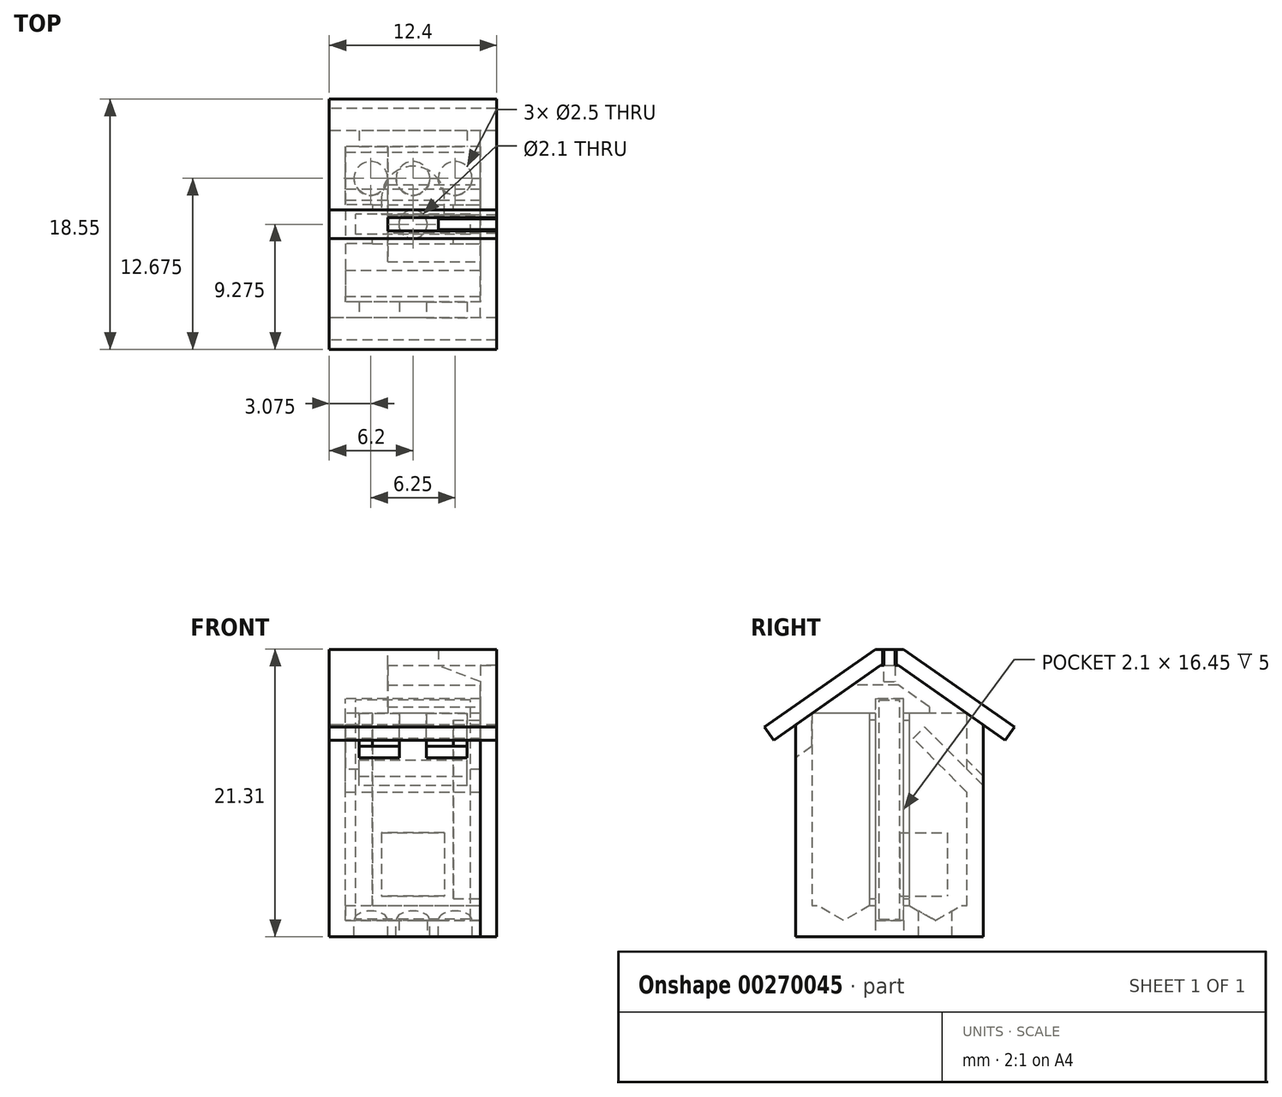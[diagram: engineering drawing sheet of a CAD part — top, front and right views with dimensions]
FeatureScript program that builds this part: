
annotation { "Feature Type Name" : "Feature", "Feature Type Description" : "" }
export const myFeature = defineFeature(function(context is Context, id is Id, definition is map)
    precondition{}
    {
        {
            var Q0;
            Q0=qCreatedBy(makeId("Top.planeOp"),FACE);
            var sketch = newSketch(context, id + "F0", { "sketchPlane" : qUnion([Q0])});
            skArc(sketch, "E0", {"start": v(2.33, 0) * mm, "mid": v(0, 2.33) * mm, "end": v(-2.33, 0) * mm});
            skLineSegment(sketch, "E1", {"start": v(-2.33, 0) * mm, "end": v(-2.33, -1.23) * mm});
            skLineSegment(sketch, "E2", {"start": v(-2.32, -1.23) * mm, "end": v(2.32, -1.22) * mm});
            skLineSegment(sketch, "E3", {"start": v(2.33, -1.23) * mm, "end": v(2.33, 0) * mm});
            skSolve(sketch);
        }
        {
            var Q0;
            Q0 = qSketchRegion(id + "F0", true);
            extrude(context, id + "F1", {"entities" : qUnion([Q0]), "endBound" : BoundingType.SYMMETRIC, "depth" : 4.7 * mm});
        }
        {
            var Q0;
            Q0=makeQuery(id+"F1.opExtrude","CAP_FACE",FACE,{"disambiguationData":[OSD([sQuery(id+"F0.wireOp",EDGE,"E0"),sQuery(id+"F0.wireOp",EDGE,"E1"),sQuery(id+"F0.wireOp",EDGE,"E2"),sQuery(id+"F0.wireOp",EDGE,"E3")])],"isStart":false});
            var sketch = newSketch(context, id + "F2", { "sketchPlane" : qUnion([Q0])});
            skLineSegment(sketch, "E4.bottom", {"start": v(1.88, 0.45) * mm, "end": v(-1.87, 0.45) * mm});
            skLineSegment(sketch, "E4.top", {"start": v(1.88, -0.45) * mm, "end": v(-1.88, -0.45) * mm});
            skLineSegment(sketch, "E4.left", {"start": v(1.88, 0.45) * mm, "end": v(1.88, -0.45) * mm});
            skLineSegment(sketch, "E4.right", {"start": v(-1.88, 0.45) * mm, "end": v(-1.88, -0.45) * mm});
            skPoint(sketch, "E4.middle", {"position": v(0, 0) * mm});
            skSolve(sketch);
        }
        {
            var Q0;
            Q0=makeQuery(id+"F1.opExtrude","SWEPT_FACE",FACE,{"disambiguationData":[OSD([sQuery(id+"F0.wireOp",EDGE,"E2")])]});
            var sketch = newSketch(context, id + "F3", { "sketchPlane" : qUnion([Q0])});
            skLineSegment(sketch, "E5.bottom", {"start": v(4.25, -4.05) * mm, "end": v(-4.25, -4.05) * mm});
            skLineSegment(sketch, "E5.top", {"start": v(4.25, 12.2) * mm, "end": v(-4.25, 12.2) * mm});
            skLineSegment(sketch, "E5.left", {"start": v(4.25, -4.05) * mm, "end": v(4.25, 12.2) * mm});
            skLineSegment(sketch, "E5.right", {"start": v(-4.25, -4.05) * mm, "end": v(-4.25, 12.2) * mm});
            skPoint(sketch, "E5.middle", {"position": v(0, 4.08) * mm});
            skSolve(sketch);
        }
        {
            var Q0;
            Q0 = qSketchRegion(id + "F3", true);
            extrude(context, id + "F4", {"entities" : qUnion([Q0]), "operationType" : NewBodyOperationType.ADD, "depth" : 1.5 * mm});
        }
        {
            var Q0;
            Q0=qCreatedBy(makeId("Right.planeOp"),FACE);
            var sketch = newSketch(context, id + "F5", { "sketchPlane" : qUnion([Q0])});
            skLineSegment(sketch, "E6", {"start": v(-3.02, -4.15) * mm, "end": v(-0.92, -4.15) * mm});
            skLineSegment(sketch, "E7", {"start": v(-0.92, -4.15) * mm, "end": v(-0.92, -3.05) * mm});
            skLineSegment(sketch, "E8", {"start": v(-0.92, -3.05) * mm, "end": v(3.78, -3.05) * mm});
            skLineSegment(sketch, "E9", {"start": v(3.78, -3.05) * mm, "end": v(3.78, 11.2) * mm});
            skLineSegment(sketch, "E10", {"start": v(3.78, 11.2) * mm, "end": v(-0.92, 11.2) * mm});
            skLineSegment(sketch, "E11", {"start": v(-0.92, 11.2) * mm, "end": v(-0.92, 12.3) * mm});
            skLineSegment(sketch, "E12", {"start": v(-0.92, 12.3) * mm, "end": v(-3.02, 12.3) * mm});
            skLineSegment(sketch, "E13", {"start": v(-3.02, 12.3) * mm, "end": v(-3.02, 11.2) * mm});
            skLineSegment(sketch, "E14", {"start": v(-3.02, 11.2) * mm, "end": v(-7.72, 11.2) * mm});
            skLineSegment(sketch, "E15", {"start": v(-7.72, 11.2) * mm, "end": v(-7.72, -3.05) * mm});
            skLineSegment(sketch, "E16", {"start": v(-7.72, -3.05) * mm, "end": v(-3.02, -3.05) * mm});
            skLineSegment(sketch, "E17", {"start": v(-3.02, -3.05) * mm, "end": v(-3.02, -4.15) * mm});
            skLineSegment(sketch, "E18", {"start": v(-3.02, 15.96) * mm, "end": v(-11.25, 10.2) * mm});
            skLineSegment(sketch, "E19", {"start": v(-11.25, 10.2) * mm, "end": v(-10.56, 9.21) * mm});
            skLineSegment(sketch, "E20", {"start": v(-10.56, 9.21) * mm, "end": v(-8.92, 10.36) * mm});
            skLineSegment(sketch, "E21", {"start": v(-8.92, 10.36) * mm, "end": v(-8.92, -5.35) * mm});
            skLineSegment(sketch, "E22", {"start": v(-8.92, -5.35) * mm, "end": v(4.98, -5.35) * mm});
            skLineSegment(sketch, "E23", {"start": v(4.98, -5.35) * mm, "end": v(4.98, 10.36) * mm});
            skLineSegment(sketch, "E24", {"start": v(4.98, 10.36) * mm, "end": v(6.61, 9.21) * mm});
            skLineSegment(sketch, "E25", {"start": v(6.61, 9.21) * mm, "end": v(7.3, 10.2) * mm});
            skLineSegment(sketch, "E26", {"start": v(7.3, 10.2) * mm, "end": v(-0.92, 15.96) * mm});
            skLineSegment(sketch, "E27", {"start": v(-0.92, 15.96) * mm, "end": v(-3.02, 15.96) * mm});
            skLineSegment(sketch, "E28", {"start": v(-8.92, 10.36) * mm, "end": v(-7.72, 11.2) * mm, "construction": true});
            skSolve(sketch);
        }
        {
            var Q0;
            Q0=makeQuery(id+"F5.imprint","IMPRINT",FACE,{"disambiguationData":[TD([[makeQuery(id+"F5.imprint","IMPRINT",EDGE,{"derivedFrom":sQuery(id+"F5.wireOp",EDGE,"E6")}),-1.0]])]});
            extrude(context, id + "F6", {"entities" : qUnion([Q0]), "endBound" : BoundingType.SYMMETRIC, "depth" : 10 * mm});
        }
        {
            var Q0;
            Q0=makeQuery(id+"F6.opExtrude","SWEPT_FACE",FACE,{"disambiguationData":[OSD([sQuery(id+"F5.wireOp",EDGE,"E19")])]});
            var sketch = newSketch(context, id + "F7", { "sketchPlane" : qUnion([Q0])});
            skLineSegment(sketch, "E29.bottom", {"start": v(-4, 13.6) * mm, "end": v(-1, 13.6) * mm});
            skLineSegment(sketch, "E29.top", {"start": v(-4, 11.6) * mm, "end": v(-1, 11.6) * mm});
            skLineSegment(sketch, "E29.left", {"start": v(-4, 13.6) * mm, "end": v(-4, 11.6) * mm});
            skLineSegment(sketch, "E29.right", {"start": v(-1, 13.6) * mm, "end": v(-1, 11.6) * mm});
            skLineSegment(sketch, "E30.bottom", {"start": v(4, 13.6) * mm, "end": v(1, 13.6) * mm});
            skLineSegment(sketch, "E30.top", {"start": v(4, 11.6) * mm, "end": v(1, 11.6) * mm});
            skLineSegment(sketch, "E30.left", {"start": v(4, 13.6) * mm, "end": v(4, 11.6) * mm});
            skLineSegment(sketch, "E30.right", {"start": v(1, 13.6) * mm, "end": v(1, 11.6) * mm});
            skSolve(sketch);
        }
        {
            var Q0;
            Q0 = qSketchRegion(id + "F7", true);
            var Q1;
            Q1=makeQuery(id+"F6.opExtrude","SWEPT_FACE",FACE,{"disambiguationData":[OSD([sQuery(id+"F5.wireOp",EDGE,"E14")])]});
            extrude(context, id + "F8", {"entities" : qUnion([Q0]), "operationType" : NewBodyOperationType.REMOVE, "endBound" : BoundingType.UP_TO_SURFACE, "oppositeDirection" : true, "endBoundEntityFace" : qUnion([Q1]), "depth" : 25 * mm});
        }
        {
            var Q0;
            Q0=makeQuery(id+"F4.opExtrude","SWEPT_EDGE",EDGE,{"disambiguationData":[OSD([sQuery(id+"F3.wireOp",EDGE,"E5.top"),sQuery(id+"F3.wireOp",EDGE,"E5.left")])]});
            cPoint(context, id + "F9", {"entities" : qUnion([Q0]), "parameter" : 0.5});
        }
        {
            var Q0;
            Q0=makeQuery(id+"F4.opExtrude","SWEPT_EDGE",EDGE,{"disambiguationData":[OSD([sQuery(id+"F3.wireOp",EDGE,"E5.bottom"),sQuery(id+"F3.wireOp",EDGE,"E5.left")])]});
            cPoint(context, id + "F10", {"entities" : qUnion([Q0]), "parameter" : 0.5});
        }
        {
            var Q0;
            Q0=makeQuery(id+"F4.opExtrude","SWEPT_EDGE",EDGE,{"disambiguationData":[OSD([sQuery(id+"F3.wireOp",EDGE,"E5.bottom"),sQuery(id+"F3.wireOp",EDGE,"E5.right")])]});
            cPoint(context, id + "F11", {"entities" : qUnion([Q0]), "parameter" : 0.5});
        }
        {
            var Q0;
            Q0 = qCreatedBy(id + "F9" ,VERTEX);
            var Q1;
            Q1 = qCreatedBy(id + "F10" ,VERTEX);
            var Q2;
            Q2 = qCreatedBy(id + "F11" ,VERTEX);
            cPlane(context, id + "F12", {"entities" : qUnion([Q0, Q1, Q2]), "cplaneType" : CPlaneType.THREE_POINT, "offset" : 25 * mm, "width" : 150 * mm, "height" : 150 * mm});
        }
        {
            var Q0;
            Q0=makeQuery(id+"F6.opExtrude","SWEPT_FACE",FACE,{"disambiguationData":[OSD([sQuery(id+"F5.wireOp",EDGE,"E16")])]});
            var sketch = newSketch(context, id + "F13", { "sketchPlane" : qUnion([Q0])});
            skCircle(sketch, "E31", {"center": v(-3.12, 1.43) * mm, "radius": 1.25 * mm});
            skCircle(sketch, "E32", {"center": v(0, 1.43) * mm, "radius": 1.25 * mm});
            skCircle(sketch, "E33", {"center": v(3.12, 1.43) * mm, "radius": 1.25 * mm});
            skLineSegment(sketch, "E34", {"start": v(-3.12, 1.43) * mm, "end": v(-5, 1.43) * mm, "construction": true});
            skLineSegment(sketch, "E35", {"start": v(-3.12, 1.43) * mm, "end": v(-1.25, 1.43) * mm, "construction": true});
            skSolve(sketch);
        }
        {
            var Q0;
            Q0 = qSketchRegion(id + "F13", true);
            extrude(context, id + "F14", {"entities" : qUnion([Q0]), "operationType" : NewBodyOperationType.REMOVE, "endBound" : BoundingType.THROUGH_ALL, "oppositeDirection" : true, "depth" : 25 * mm});
        }
        {
            var Q0;
            Q0=makeQuery(id+"F6.opExtrude","CAP_FACE",FACE,{"disambiguationData":[OSD([sQuery(id+"F5.wireOp",EDGE,"E6"),sQuery(id+"F5.wireOp",EDGE,"E7"),sQuery(id+"F5.wireOp",EDGE,"E8"),sQuery(id+"F5.wireOp",EDGE,"E9"),sQuery(id+"F5.wireOp",EDGE,"E10"),sQuery(id+"F5.wireOp",EDGE,"E11"),sQuery(id+"F5.wireOp",EDGE,"E12"),sQuery(id+"F5.wireOp",EDGE,"E13"),sQuery(id+"F5.wireOp",EDGE,"E14"),sQuery(id+"F5.wireOp",EDGE,"E15"),sQuery(id+"F5.wireOp",EDGE,"E16"),sQuery(id+"F5.wireOp",EDGE,"E17"),sQuery(id+"F5.wireOp",EDGE,"E18"),sQuery(id+"F5.wireOp",EDGE,"E19"),sQuery(id+"F5.wireOp",EDGE,"E20"),sQuery(id+"F5.wireOp",EDGE,"E21"),sQuery(id+"F5.wireOp",EDGE,"E22"),sQuery(id+"F5.wireOp",EDGE,"E23"),sQuery(id+"F5.wireOp",EDGE,"E24"),sQuery(id+"F5.wireOp",EDGE,"E25"),sQuery(id+"F5.wireOp",EDGE,"E26"),sQuery(id+"F5.wireOp",EDGE,"E27")])],"isStart":true});
            var sketch = newSketch(context, id + "F15", { "sketchPlane" : qUnion([Q0])});
            skLineSegment(sketch, "E36.0.0", {"start": v(0.92, 15.96) * mm, "end": v(-7.3, 10.2) * mm});
            skLineSegment(sketch, "E36.0.1", {"start": v(-7.3, 10.2) * mm, "end": v(-6.61, 9.21) * mm});
            skLineSegment(sketch, "E36.0.2", {"start": v(-6.61, 9.21) * mm, "end": v(-4.98, 10.36) * mm});
            skLineSegment(sketch, "E36.0.3", {"start": v(-4.98, 10.36) * mm, "end": v(-4.98, -5.35) * mm});
            skLineSegment(sketch, "E36.0.4", {"start": v(-4.98, -5.35) * mm, "end": v(8.92, -5.35) * mm});
            skLineSegment(sketch, "E36.0.5", {"start": v(8.92, -5.35) * mm, "end": v(8.92, 10.36) * mm});
            skLineSegment(sketch, "E36.0.6", {"start": v(8.92, 10.36) * mm, "end": v(10.56, 9.21) * mm});
            skLineSegment(sketch, "E36.0.7", {"start": v(10.56, 9.21) * mm, "end": v(11.25, 10.2) * mm});
            skLineSegment(sketch, "E36.0.8", {"start": v(11.25, 10.2) * mm, "end": v(3.02, 15.96) * mm});
            skLineSegment(sketch, "E36.0.9", {"start": v(3.02, 15.96) * mm, "end": v(0.92, 15.96) * mm});
            skSolve(sketch);
        }
        {
            var Q0;
            Q0 = qSketchRegion(id + "F15", true);
            extrude(context, id + "F16", {"entities" : qUnion([Q0]), "operationType" : NewBodyOperationType.ADD, "depth" : 1.2 * mm});
        }
        {
            var Q0;
            Q0=makeQuery(id+"F6.opExtrude","CAP_FACE",FACE,{"disambiguationData":[OSD([sQuery(id+"F5.wireOp",EDGE,"E6"),sQuery(id+"F5.wireOp",EDGE,"E7"),sQuery(id+"F5.wireOp",EDGE,"E8"),sQuery(id+"F5.wireOp",EDGE,"E9"),sQuery(id+"F5.wireOp",EDGE,"E10"),sQuery(id+"F5.wireOp",EDGE,"E11"),sQuery(id+"F5.wireOp",EDGE,"E12"),sQuery(id+"F5.wireOp",EDGE,"E13"),sQuery(id+"F5.wireOp",EDGE,"E14"),sQuery(id+"F5.wireOp",EDGE,"E15"),sQuery(id+"F5.wireOp",EDGE,"E16"),sQuery(id+"F5.wireOp",EDGE,"E17"),sQuery(id+"F5.wireOp",EDGE,"E18"),sQuery(id+"F5.wireOp",EDGE,"E19"),sQuery(id+"F5.wireOp",EDGE,"E20"),sQuery(id+"F5.wireOp",EDGE,"E21"),sQuery(id+"F5.wireOp",EDGE,"E22"),sQuery(id+"F5.wireOp",EDGE,"E23"),sQuery(id+"F5.wireOp",EDGE,"E24"),sQuery(id+"F5.wireOp",EDGE,"E25"),sQuery(id+"F5.wireOp",EDGE,"E26"),sQuery(id+"F5.wireOp",EDGE,"E27")])],"isStart":false});
            var sketch = newSketch(context, id + "F17", { "sketchPlane" : qUnion([Q0])});
            skLineSegment(sketch, "E37", {"start": v(-3.02, 15.96) * mm, "end": v(-11.25, 10.2) * mm});
            skLineSegment(sketch, "E38", {"start": v(-11.25, 10.2) * mm, "end": v(-10.56, 9.21) * mm});
            skLineSegment(sketch, "E39", {"start": v(-10.56, 9.21) * mm, "end": v(-2.65, 14.76) * mm});
            skLineSegment(sketch, "E40", {"start": v(-2.65, 14.76) * mm, "end": v(-1.3, 14.76) * mm});
            skLineSegment(sketch, "E41", {"start": v(-1.3, 14.76) * mm, "end": v(6.61, 9.21) * mm});
            skLineSegment(sketch, "E42", {"start": v(6.61, 9.21) * mm, "end": v(7.3, 10.2) * mm});
            skLineSegment(sketch, "E43", {"start": v(7.3, 10.2) * mm, "end": v(-0.92, 15.96) * mm});
            skLineSegment(sketch, "E44", {"start": v(-0.92, 15.96) * mm, "end": v(-3.02, 15.96) * mm});
            skSolve(sketch);
        }
        {
            var Q0;
            Q0 = qSketchRegion(id + "F17", true);
            extrude(context, id + "F18", {"entities" : qUnion([Q0]), "operationType" : NewBodyOperationType.ADD, "depth" : 1.2 * mm});
        }
        {
            var Q0;
            {var subQ0=sQuery(id+"F5.wireOp",EDGE,"E24");var subQ1=sQuery(id+"F5.wireOp",EDGE,"E20");var subQ2=sQuery(id+"F5.wireOp",EDGE,"E14");var subQ3=sQuery(id+"F5.wireOp",EDGE,"E13");var subQ4=sQuery(id+"F5.wireOp",EDGE,"E12");var subQ5=sQuery(id+"F5.wireOp",EDGE,"E15");var subQ6=sQuery(id+"F5.wireOp",EDGE,"E11");var subQ7=sQuery(id+"F5.wireOp",EDGE,"E10");var subQ8=sQuery(id+"F5.wireOp",EDGE,"E9");var subQ9=makeQuery(id+"F6.opExtrude","CAP_FACE",FACE,{"disambiguationData":[OSD([sQuery(id+"F5.wireOp",EDGE,"E6"),sQuery(id+"F5.wireOp",EDGE,"E7"),sQuery(id+"F5.wireOp",EDGE,"E8"),subQ8,subQ7,subQ6,subQ4,subQ3,subQ2,subQ5,sQuery(id+"F5.wireOp",EDGE,"E16"),sQuery(id+"F5.wireOp",EDGE,"E17"),sQuery(id+"F5.wireOp",EDGE,"E18"),sQuery(id+"F5.wireOp",EDGE,"E19"),subQ1,sQuery(id+"F5.wireOp",EDGE,"E21"),sQuery(id+"F5.wireOp",EDGE,"E22"),sQuery(id+"F5.wireOp",EDGE,"E23"),subQ0,sQuery(id+"F5.wireOp",EDGE,"E25"),sQuery(id+"F5.wireOp",EDGE,"E26"),sQuery(id+"F5.wireOp",EDGE,"E27")])],"isStart":false});Q0=makeQuery(id+"F18.boolean.opBoolean","SPLIT",FACE,{"disambiguationData":[TD([makeQuery(id+"F6.opExtrude","SWEPT_FACE",FACE,{"disambiguationData":[OSD([subQ6])]})])],"derivedFrom":subQ9});}
            var sketch = newSketch(context, id + "F19", { "sketchPlane" : qUnion([Q0])});
            skLineSegment(sketch, "E45", {"start": v(-4.74, 13.3) * mm, "end": v(-2.65, 14.76) * mm});
            skLineSegment(sketch, "E46", {"start": v(-2.65, 14.76) * mm, "end": v(-2.47, 14.76) * mm});
            skLineSegment(sketch, "E47", {"start": v(-2.47, 14.76) * mm, "end": v(-2.47, 15.96) * mm});
            skLineSegment(sketch, "E48", {"start": v(-2.47, 15.96) * mm, "end": v(-1.47, 15.96) * mm});
            skLineSegment(sketch, "E49", {"start": v(-1.47, 15.96) * mm, "end": v(-1.47, 14.76) * mm});
            skLineSegment(sketch, "E50", {"start": v(-1.47, 14.76) * mm, "end": v(-1.3, 14.76) * mm});
            skLineSegment(sketch, "E51", {"start": v(-1.3, 14.76) * mm, "end": v(3.78, 11.2) * mm});
            skLineSegment(sketch, "E52", {"start": v(3.78, 11.2) * mm, "end": v(0.97, 11.2) * mm});
            skLineSegment(sketch, "E53", {"start": v(0.97, 11.7) * mm, "end": v(-1.3, 13.3) * mm});
            skLineSegment(sketch, "E54", {"start": v(-1.3, 13.3) * mm, "end": v(-4.74, 13.3) * mm});
            skLineSegment(sketch, "E55", {"start": v(0.97, 11.7) * mm, "end": v(0.97, 11.2) * mm});
            skSolve(sketch);
        }
        {
            var Q0;
            Q0 = qSketchRegion(id + "F19", true);
            var Q1;
            Q1=sQuery(id+"F2.wireOp",VERTEX,"E4.right.start");
            var Q2;
            Q2=makeQuery(id+"F18.opExtrude","CAP_VERTEX",VERTEX,{"disambiguationData":[OSD([sQuery(id+"F17.wireOp",EDGE,"E43"),sQuery(id+"F17.wireOp",EDGE,"E44")])],"isStart":false});
            extrude(context, id + "F20", {"entities" : qUnion([Q0]), "operationType" : NewBodyOperationType.REMOVE, "endBound" : BoundingType.UP_TO_VERTEX, "oppositeDirection" : true, "endBoundEntityVertex" : qUnion([Q1]), "depth" : 25 * mm, "hasSecondDirection" : true, "secondDirectionBound" : SecondDirectionBoundingType.UP_TO_VERTEX, "secondDirectionOppositeDirection" : false, "secondDirectionBoundEntityVertex" : qUnion([Q2]), "secondDirectionDepth" : 25 * mm});
        }
        {
            var Q0;
            Q0=makeQuery(id+"F16.opExtrude","CAP_FACE",FACE,{"disambiguationData":[OSD([sQuery(id+"F15.wireOp",EDGE,"E36.0.0"),sQuery(id+"F15.wireOp",EDGE,"E36.0.1"),sQuery(id+"F15.wireOp",EDGE,"E36.0.2"),sQuery(id+"F15.wireOp",EDGE,"E36.0.3"),sQuery(id+"F15.wireOp",EDGE,"E36.0.4"),sQuery(id+"F15.wireOp",EDGE,"E36.0.5"),sQuery(id+"F15.wireOp",EDGE,"E36.0.6"),sQuery(id+"F15.wireOp",EDGE,"E36.0.7"),sQuery(id+"F15.wireOp",EDGE,"E36.0.8"),sQuery(id+"F15.wireOp",EDGE,"E36.0.9")])],"isStart":true});
            var sketch = newSketch(context, id + "F21", { "sketchPlane" : qUnion([Q0])});
            skLineSegment(sketch, "E56", {"start": v(0.62, 10.2) * mm, "end": v(3.78, 7.05) * mm});
            skLineSegment(sketch, "E57", {"start": v(3.78, 7.05) * mm, "end": v(3.78, 5.35) * mm});
            skLineSegment(sketch, "E58", {"start": v(3.78, 5.35) * mm, "end": v(-0.22, 9.35) * mm});
            skLineSegment(sketch, "E59", {"start": v(-0.22, 9.35) * mm, "end": v(0.62, 10.2) * mm});
            skSolve(sketch);
        }
        {
            var Q0;
            Q0=makeQuery(id+"F21.imprint","IMPRINT",FACE,{"disambiguationData":[TD([[makeQuery(id+"F21.imprint","IMPRINT",EDGE,{"derivedFrom":sQuery(id+"F21.wireOp",EDGE,"E56")}),-1.0]])]});
            var Q1;
            {var subQ0=sQuery(id+"F5.wireOp",EDGE,"E24");var subQ1=sQuery(id+"F5.wireOp",EDGE,"E20");var subQ2=sQuery(id+"F5.wireOp",EDGE,"E14");var subQ3=sQuery(id+"F5.wireOp",EDGE,"E13");var subQ4=sQuery(id+"F5.wireOp",EDGE,"E12");var subQ5=sQuery(id+"F5.wireOp",EDGE,"E15");var subQ6=sQuery(id+"F5.wireOp",EDGE,"E11");var subQ7=sQuery(id+"F5.wireOp",EDGE,"E10");var subQ8=sQuery(id+"F5.wireOp",EDGE,"E9");var subQ9=makeQuery(id+"F6.opExtrude","CAP_FACE",FACE,{"disambiguationData":[OSD([sQuery(id+"F5.wireOp",EDGE,"E6"),sQuery(id+"F5.wireOp",EDGE,"E7"),sQuery(id+"F5.wireOp",EDGE,"E8"),subQ8,subQ7,subQ6,subQ4,subQ3,subQ2,subQ5,sQuery(id+"F5.wireOp",EDGE,"E16"),sQuery(id+"F5.wireOp",EDGE,"E17"),sQuery(id+"F5.wireOp",EDGE,"E18"),sQuery(id+"F5.wireOp",EDGE,"E19"),subQ1,sQuery(id+"F5.wireOp",EDGE,"E21"),sQuery(id+"F5.wireOp",EDGE,"E22"),sQuery(id+"F5.wireOp",EDGE,"E23"),subQ0,sQuery(id+"F5.wireOp",EDGE,"E25"),sQuery(id+"F5.wireOp",EDGE,"E26"),sQuery(id+"F5.wireOp",EDGE,"E27")])],"isStart":false});Q1=makeQuery(id+"F18.boolean.opBoolean","SPLIT",FACE,{"disambiguationData":[TD([makeQuery(id+"F6.opExtrude","SWEPT_FACE",FACE,{"disambiguationData":[OSD([subQ6])]})])],"derivedFrom":subQ9});}
            extrude(context, id + "F22", {"entities" : qUnion([Q0]), "operationType" : NewBodyOperationType.ADD, "endBound" : BoundingType.UP_TO_SURFACE, "endBoundEntityFace" : qUnion([Q1]), "depth" : 25 * mm});
        }
        {
            var Q0;
            {var subQ1=sQuery(id+"F5.wireOp",EDGE,"E22");var subQ3=sQuery(id+"F5.wireOp",EDGE,"E24");var subQ4=sQuery(id+"F5.wireOp",EDGE,"E23");var subQ5=sQuery(id+"F5.wireOp",EDGE,"E21");var subQ6=sQuery(id+"F5.wireOp",EDGE,"E20");var subQ7=sQuery(id+"F5.wireOp",EDGE,"E17");var subQ8=sQuery(id+"F5.wireOp",EDGE,"E16");var subQ9=sQuery(id+"F5.wireOp",EDGE,"E15");var subQ10=sQuery(id+"F5.wireOp",EDGE,"E14");var subQ11=sQuery(id+"F5.wireOp",EDGE,"E10");var subQ12=sQuery(id+"F5.wireOp",EDGE,"E9");var subQ13=sQuery(id+"F5.wireOp",EDGE,"E8");var subQ14=sQuery(id+"F5.wireOp",EDGE,"E7");var subQ15=sQuery(id+"F5.wireOp",EDGE,"E6");var subQ16=makeQuery(id+"F6.opExtrude","CAP_FACE",FACE,{"disambiguationData":[OSD([subQ15,subQ14,subQ13,subQ12,subQ11,sQuery(id+"F5.wireOp",EDGE,"E11"),sQuery(id+"F5.wireOp",EDGE,"E12"),sQuery(id+"F5.wireOp",EDGE,"E13"),subQ10,subQ9,subQ8,subQ7,sQuery(id+"F5.wireOp",EDGE,"E18"),sQuery(id+"F5.wireOp",EDGE,"E19"),subQ6,subQ5,subQ1,subQ4,subQ3,sQuery(id+"F5.wireOp",EDGE,"E25"),sQuery(id+"F5.wireOp",EDGE,"E26"),sQuery(id+"F5.wireOp",EDGE,"E27")])],"isStart":false});Q0=makeQuery(id+"F22.boolean.opBoolean","MERGE",FACE,{"derivedFrom":[makeQuery(id+"F18.boolean.opBoolean","SPLIT",FACE,{"disambiguationData":[TD([makeQuery(id+"F6.opExtrude","SWEPT_FACE",FACE,{"disambiguationData":[OSD([subQ15])]})])],"derivedFrom":subQ16}),makeQuery(id+"F22.opExtrude","CAP_FACE",FACE,{"disambiguationData":[OSD([sQuery(id+"F21.wireOp",EDGE,"E56"),sQuery(id+"F21.wireOp",EDGE,"E57"),sQuery(id+"F21.wireOp",EDGE,"E58"),sQuery(id+"F21.wireOp",EDGE,"E59")])],"isStart":false})]});}
            var sketch = newSketch(context, id + "F23", { "sketchPlane" : qUnion([Q0])});
            skLineSegment(sketch, "E60.0", {"start": v(-8.92, 10.36) * mm, "end": v(-8.92, -5.35) * mm});
            skLineSegment(sketch, "E61.0", {"start": v(-8.92, -5.35) * mm, "end": v(4.98, -5.35) * mm});
            skLineSegment(sketch, "E62.0", {"start": v(4.98, -5.35) * mm, "end": v(4.98, 10.36) * mm});
            skLineSegment(sketch, "E63", {"start": v(-8.92, 10.36) * mm, "end": v(-2.65, 14.76) * mm});
            skLineSegment(sketch, "E64", {"start": v(-1.3, 14.76) * mm, "end": v(4.98, 10.36) * mm});
            skLineSegment(sketch, "E65", {"start": v(-2.65, 14.76) * mm, "end": v(-2.37, 14.76) * mm});
            skLineSegment(sketch, "E66", {"start": v(-2.37, 14.76) * mm, "end": v(-2.37, 15.96) * mm});
            skLineSegment(sketch, "E67", {"start": v(-2.37, 15.96) * mm, "end": v(-1.57, 15.96) * mm});
            skLineSegment(sketch, "E68", {"start": v(-1.57, 15.96) * mm, "end": v(-1.57, 14.76) * mm});
            skLineSegment(sketch, "E69", {"start": v(-1.57, 14.76) * mm, "end": v(-1.3, 14.76) * mm});
            skSolve(sketch);
        }
        {
            var Q0;
            Q0 = qSketchRegion(id + "F23", true);
            var Q1;
            {var subQ0=sQuery(id+"F17.wireOp",EDGE,"E42");var subQ1=sQuery(id+"F17.wireOp",EDGE,"E40");var subQ2=sQuery(id+"F17.wireOp",EDGE,"E41");var subQ3=sQuery(id+"F17.wireOp",EDGE,"E43");var subQ4=sQuery(id+"F17.wireOp",EDGE,"E44");Q1=makeQuery(id+"F20.boolean.opBoolean","SPLIT",FACE,{"disambiguationData":[TD([makeQuery(id+"F6.opExtrude","SWEPT_FACE",FACE,{"disambiguationData":[OSD([sQuery(id+"F5.wireOp",EDGE,"E24")])]})])],"derivedFrom":makeQuery(id+"F18.opExtrude","CAP_FACE",FACE,{"disambiguationData":[OSD([sQuery(id+"F17.wireOp",EDGE,"E37"),sQuery(id+"F17.wireOp",EDGE,"E38"),sQuery(id+"F17.wireOp",EDGE,"E39"),subQ1,subQ2,subQ0,subQ3,subQ4])],"isStart":false})});}
            extrude(context, id + "F24", {"entities" : qUnion([Q0]), "endBound" : BoundingType.UP_TO_SURFACE, "endBoundEntityFace" : qUnion([Q1]), "depth" : 25 * mm});
        }
        {
            var Q0;
            Q0=makeQuery(id+"F24.opExtrude","CAP_FACE",FACE,{"disambiguationData":[OSD([sQuery(id+"F23.wireOp",EDGE,"E60.0"),sQuery(id+"F23.wireOp",EDGE,"E61.0"),sQuery(id+"F23.wireOp",EDGE,"E62.0"),sQuery(id+"F23.wireOp",EDGE,"E63"),sQuery(id+"F23.wireOp",EDGE,"E64"),sQuery(id+"F23.wireOp",EDGE,"E65"),sQuery(id+"F23.wireOp",EDGE,"E66"),sQuery(id+"F23.wireOp",EDGE,"E67"),sQuery(id+"F23.wireOp",EDGE,"E68"),sQuery(id+"F23.wireOp",EDGE,"E69")])],"isStart":true});
            var sketch = newSketch(context, id + "F25", { "sketchPlane" : qUnion([Q0])});
            skLineSegment(sketch, "E70.bottom", {"start": v(2.37, 14.76) * mm, "end": v(1.57, 14.76) * mm});
            skLineSegment(sketch, "E70.top", {"start": v(2.37, 15.96) * mm, "end": v(1.57, 15.96) * mm});
            skLineSegment(sketch, "E70.left", {"start": v(2.37, 14.76) * mm, "end": v(2.37, 15.96) * mm});
            skLineSegment(sketch, "E70.right", {"start": v(1.57, 14.76) * mm, "end": v(1.57, 15.96) * mm});
            skSolve(sketch);
        }
        {
            var Q0;
            Q0 = qSketchRegion(id + "F25", true);
            var Q1;
            Q1=sQuery(id+"F2.wireOp",VERTEX,"E4.left.end");
            extrude(context, id + "F26", {"entities" : qUnion([Q0]), "operationType" : NewBodyOperationType.ADD, "endBound" : BoundingType.UP_TO_VERTEX, "endBoundEntityVertex" : qUnion([Q1]), "depth" : 25 * mm});
        }
        {
            var Q0;
            Q0=makeQuery(id+"F22.opExtrude","SWEPT_FACE",FACE,{"disambiguationData":[OSD([sQuery(id+"F21.wireOp",EDGE,"E59")])]});
            var sketch = newSketch(context, id + "F27", { "sketchPlane" : qUnion([Q0])});
            skLineSegment(sketch, "E71.bottom", {"start": v(-4, 7.65) * mm, "end": v(4, 7.65) * mm});
            skLineSegment(sketch, "E71.top", {"start": v(-4, 8.15) * mm, "end": v(4, 8.15) * mm});
            skLineSegment(sketch, "E71.left", {"start": v(-4, 7.65) * mm, "end": v(-4, 8.15) * mm});
            skLineSegment(sketch, "E71.right", {"start": v(4, 7.65) * mm, "end": v(4, 8.15) * mm});
            skSolve(sketch);
        }
        {
            var Q0;
            Q0 = qSketchRegion(id + "F27", true);
            extrude(context, id + "F28", {"entities" : qUnion([Q0]), "operationType" : NewBodyOperationType.REMOVE, "endBound" : BoundingType.THROUGH_ALL, "oppositeDirection" : true, "depth" : 25 * mm});
        }
        {
            var Q0;
            {var subQ1=sQuery(id+"F5.wireOp",EDGE,"E22");var subQ3=sQuery(id+"F5.wireOp",EDGE,"E24");var subQ4=sQuery(id+"F5.wireOp",EDGE,"E23");var subQ5=sQuery(id+"F5.wireOp",EDGE,"E21");var subQ6=sQuery(id+"F5.wireOp",EDGE,"E20");var subQ7=sQuery(id+"F5.wireOp",EDGE,"E17");var subQ8=sQuery(id+"F5.wireOp",EDGE,"E16");var subQ9=sQuery(id+"F5.wireOp",EDGE,"E15");var subQ10=sQuery(id+"F5.wireOp",EDGE,"E14");var subQ11=sQuery(id+"F5.wireOp",EDGE,"E10");var subQ12=sQuery(id+"F5.wireOp",EDGE,"E9");var subQ13=sQuery(id+"F5.wireOp",EDGE,"E8");var subQ14=sQuery(id+"F5.wireOp",EDGE,"E7");var subQ15=sQuery(id+"F5.wireOp",EDGE,"E6");var subQ16=makeQuery(id+"F6.opExtrude","CAP_FACE",FACE,{"disambiguationData":[OSD([subQ15,subQ14,subQ13,subQ12,subQ11,sQuery(id+"F5.wireOp",EDGE,"E11"),sQuery(id+"F5.wireOp",EDGE,"E12"),sQuery(id+"F5.wireOp",EDGE,"E13"),subQ10,subQ9,subQ8,subQ7,sQuery(id+"F5.wireOp",EDGE,"E18"),sQuery(id+"F5.wireOp",EDGE,"E19"),subQ6,subQ5,subQ1,subQ4,subQ3,sQuery(id+"F5.wireOp",EDGE,"E25"),sQuery(id+"F5.wireOp",EDGE,"E26"),sQuery(id+"F5.wireOp",EDGE,"E27")])],"isStart":false});Q0=makeQuery(id+"F22.boolean.opBoolean","MERGE",FACE,{"derivedFrom":[makeQuery(id+"F18.boolean.opBoolean","SPLIT",FACE,{"disambiguationData":[TD([makeQuery(id+"F6.opExtrude","SWEPT_FACE",FACE,{"disambiguationData":[OSD([subQ15])]})])],"derivedFrom":subQ16}),makeQuery(id+"F22.opExtrude","CAP_FACE",FACE,{"disambiguationData":[OSD([sQuery(id+"F21.wireOp",EDGE,"E56"),sQuery(id+"F21.wireOp",EDGE,"E57"),sQuery(id+"F21.wireOp",EDGE,"E58"),sQuery(id+"F21.wireOp",EDGE,"E59")])],"isStart":false})]});}
            var sketch = newSketch(context, id + "F29", { "sketchPlane" : qUnion([Q0])});
            skLineSegment(sketch, "E72", {"start": v(-7.33, -3.05) * mm, "end": v(-3.42, -3.05) * mm});
            skLineSegment(sketch, "E73", {"start": v(-3.42, -3.05) * mm, "end": v(-5.37, -4.15) * mm});
            skLineSegment(sketch, "E74", {"start": v(-5.37, -4.15) * mm, "end": v(-7.33, -3.05) * mm});
            skPoint(sketch, "E75", {"position": v(-5.37, -3.05) * mm});
            skLineSegment(sketch, "E76.MirrorCS", {"start": v(-0.52, -3.05) * mm, "end": v(1.43, -4.15) * mm});
            skLineSegment(sketch, "E77.MirrorCS", {"start": v(1.43, -4.15) * mm, "end": v(3.38, -3.05) * mm});
            skLineSegment(sketch, "E78.MirrorCS", {"start": v(3.38, -3.05) * mm, "end": v(-0.52, -3.05) * mm});
            skSolve(sketch);
        }
        {
            var Q0;
            Q0 = qSketchRegion(id + "F29", true);
            var Q1;
            Q1=makeQuery(id+"F16.opExtrude","CAP_FACE",FACE,{"disambiguationData":[OSD([sQuery(id+"F15.wireOp",EDGE,"E36.0.0"),sQuery(id+"F15.wireOp",EDGE,"E36.0.1"),sQuery(id+"F15.wireOp",EDGE,"E36.0.2"),sQuery(id+"F15.wireOp",EDGE,"E36.0.3"),sQuery(id+"F15.wireOp",EDGE,"E36.0.4"),sQuery(id+"F15.wireOp",EDGE,"E36.0.5"),sQuery(id+"F15.wireOp",EDGE,"E36.0.6"),sQuery(id+"F15.wireOp",EDGE,"E36.0.7"),sQuery(id+"F15.wireOp",EDGE,"E36.0.8"),sQuery(id+"F15.wireOp",EDGE,"E36.0.9")])],"isStart":true});
            extrude(context, id + "F30", {"entities" : qUnion([Q0]), "operationType" : NewBodyOperationType.REMOVE, "endBound" : BoundingType.UP_TO_SURFACE, "oppositeDirection" : true, "endBoundEntityFace" : qUnion([Q1]), "depth" : 25 * mm});
        }
        {
            var Q0;
            Q0=makeQuery(id+"F16.boolean.opBoolean","MERGE",FACE,{"derivedFrom":[makeQuery(id+"F6.opExtrude","SWEPT_FACE",FACE,{"disambiguationData":[OSD([sQuery(id+"F5.wireOp",EDGE,"E22")])]}),makeQuery(id+"F16.opExtrude","SWEPT_FACE",FACE,{"disambiguationData":[OSD([sQuery(id+"F15.wireOp",EDGE,"E36.0.4")])]})]});
            var sketch = newSketch(context, id + "F31", { "sketchPlane" : qUnion([Q0])});
            skCircle(sketch, "E79", {"center": v(0, 1.97) * mm, "radius": 1.05 * mm});
            skPoint(sketch, "E79.centerSnap0", {"position": v(-6.2, 1.97) * mm});
            skSolve(sketch);
        }
        {
            var Q0;
            Q0 = qSketchRegion(id + "F31", true);
            var Q1;
            Q1=makeQuery(id+"F6.opExtrude","SWEPT_FACE",FACE,{"disambiguationData":[OSD([sQuery(id+"F5.wireOp",EDGE,"E6")])]});
            extrude(context, id + "F32", {"entities" : qUnion([Q0]), "operationType" : NewBodyOperationType.REMOVE, "endBound" : BoundingType.UP_TO_SURFACE, "oppositeDirection" : true, "endBoundEntityFace" : qUnion([Q1]), "depth" : 25 * mm});
        }
        {
            var Q0;
            {var subQ0=sQuery(id+"F15.wireOp",EDGE,"E36.0.9");var subQ1=sQuery(id+"F15.wireOp",EDGE,"E36.0.8");var subQ2=sQuery(id+"F15.wireOp",EDGE,"E36.0.7");var subQ3=sQuery(id+"F15.wireOp",EDGE,"E36.0.6");var subQ4=sQuery(id+"F15.wireOp",EDGE,"E36.0.5");var subQ5=sQuery(id+"F15.wireOp",EDGE,"E36.0.4");var subQ6=sQuery(id+"F15.wireOp",EDGE,"E36.0.3");var subQ7=sQuery(id+"F15.wireOp",EDGE,"E36.0.2");var subQ8=sQuery(id+"F15.wireOp",EDGE,"E36.0.1");var subQ9=sQuery(id+"F15.wireOp",EDGE,"E36.0.0");Q0=makeQuery(id+"F30.boolean.opBoolean","MERGE",FACE,{"derivedFrom":[makeQuery(id+"F16.opExtrude","CAP_FACE",FACE,{"disambiguationData":[OSD([subQ9,subQ8,subQ7,subQ6,subQ5,subQ4,subQ3,subQ2,subQ1,subQ0])],"isStart":true}),makeQuery(id+"F30.opExtrude","CAP_FACE",FACE,{"disambiguationData":[OSD([subQ9,subQ8,subQ7,subQ6,subQ5,subQ4,subQ3,subQ2,subQ1,subQ0]),ownerDisambiguation([makeQuery(id+"F30.opExtrude","SWEPT_BODY",BODY,{"disambiguationData":[OSD([sQuery(id+"F29.wireOp",EDGE,"E72"),sQuery(id+"F29.wireOp",EDGE,"E73"),sQuery(id+"F29.wireOp",EDGE,"E74")])]})])],"isStart":false}),makeQuery(id+"F30.opExtrude","CAP_FACE",FACE,{"disambiguationData":[OSD([subQ9,subQ8,subQ7,subQ6,subQ5,subQ4,subQ3,subQ2,subQ1,subQ0]),ownerDisambiguation([makeQuery(id+"F30.opExtrude","SWEPT_BODY",BODY,{"disambiguationData":[OSD([sQuery(id+"F29.wireOp",EDGE,"E76.MirrorCS"),sQuery(id+"F29.wireOp",EDGE,"E77.MirrorCS"),sQuery(id+"F29.wireOp",EDGE,"E78.MirrorCS")])]})])],"isStart":false})]});}
            var sketch = newSketch(context, id + "F33", { "sketchPlane" : qUnion([Q0])});
            skLineSegment(sketch, "E80", {"start": v(-3.02, -3.05) * mm, "end": v(-3.42, -3.05) * mm});
            skLineSegment(sketch, "E81", {"start": v(-3.42, -3.05) * mm, "end": v(-3.42, 11.2) * mm});
            skLineSegment(sketch, "E82", {"start": v(-3.42, 11.2) * mm, "end": v(-3.02, 11.2) * mm});
            skLineSegment(sketch, "E83", {"start": v(-3.02, 11.2) * mm, "end": v(-3.02, -3.05) * mm});
            skLineSegment(sketch, "E84", {"start": v(-0.92, -3.05) * mm, "end": v(-0.92, 11.2) * mm});
            skLineSegment(sketch, "E85", {"start": v(-0.92, 11.2) * mm, "end": v(-0.52, 11.2) * mm});
            skLineSegment(sketch, "E86", {"start": v(-0.52, 11.2) * mm, "end": v(-0.52, -3.05) * mm});
            skLineSegment(sketch, "E87", {"start": v(-0.52, -3.05) * mm, "end": v(-0.92, -3.05) * mm});
            skSolve(sketch);
        }
        {
            var Q0;
            Q0 = qSketchRegion(id + "F33", true);
            extrude(context, id + "F34", {"entities" : qUnion([Q0]), "operationType" : NewBodyOperationType.ADD, "depth" : 2 * mm});
        }
        {
            var Q0;
            Q0=makeQuery(id+"F24.opExtrude","CAP_FACE",FACE,{"disambiguationData":[OSD([sQuery(id+"F23.wireOp",EDGE,"E60.0"),sQuery(id+"F23.wireOp",EDGE,"E61.0"),sQuery(id+"F23.wireOp",EDGE,"E62.0"),sQuery(id+"F23.wireOp",EDGE,"E63"),sQuery(id+"F23.wireOp",EDGE,"E64"),sQuery(id+"F23.wireOp",EDGE,"E65"),sQuery(id+"F23.wireOp",EDGE,"E66"),sQuery(id+"F23.wireOp",EDGE,"E67"),sQuery(id+"F23.wireOp",EDGE,"E68"),sQuery(id+"F23.wireOp",EDGE,"E69")])],"isStart":true});
            var sketch = newSketch(context, id + "F35", { "sketchPlane" : qUnion([Q0])});
            skLineSegment(sketch, "E88.0", {"start": v(3.42, -2.55) * mm, "end": v(3.42, 10.7) * mm});
            skLineSegment(sketch, "E89.0", {"start": v(3.02, 10.7) * mm, "end": v(3.02, -2.55) * mm});
            skLineSegment(sketch, "E90.0", {"start": v(0.92, -2.55) * mm, "end": v(0.92, 10.7) * mm});
            skLineSegment(sketch, "E91.0", {"start": v(0.52, 10.7) * mm, "end": v(0.52, -2.55) * mm});
            skLineSegment(sketch, "E92", {"start": v(3.42, -2.55) * mm, "end": v(3.02, -2.55) * mm});
            skLineSegment(sketch, "E93", {"start": v(0.92, -2.55) * mm, "end": v(0.52, -2.55) * mm});
            skLineSegment(sketch, "E94", {"start": v(0.92, 10.7) * mm, "end": v(0.52, 10.7) * mm});
            skLineSegment(sketch, "E95", {"start": v(3.02, 10.7) * mm, "end": v(3.42, 10.7) * mm});
            skSolve(sketch);
        }
        {
            var Q0;
            Q0 = qSketchRegion(id + "F35", true);
            extrude(context, id + "F36", {"entities" : qUnion([Q0]), "operationType" : NewBodyOperationType.ADD, "depth" : 2 * mm});
        }
        {
            var Q0;
            Q0=makeQuery(id+"F26.boolean.opBoolean","MERGE",FACE,{"derivedFrom":[makeQuery(id+"F24.opExtrude","SWEPT_FACE",FACE,{"disambiguationData":[OSD([sQuery(id+"F23.wireOp",EDGE,"E68")])]}),makeQuery(id+"F26.opExtrude","SWEPT_FACE",FACE,{"disambiguationData":[OSD([sQuery(id+"F25.wireOp",EDGE,"E70.right")])]})]});
            var sketch = newSketch(context, id + "F37", { "sketchPlane" : qUnion([Q0])});
            skLineSegment(sketch, "E96", {"start": v(-1.87, 14.76) * mm, "end": v(-5, 14.76) * mm});
            skLineSegment(sketch, "E97", {"start": v(-5, 14.76) * mm, "end": v(-5, 13.56) * mm});
            skLineSegment(sketch, "E98", {"start": v(-5, 13.56) * mm, "end": v(-1.87, 14.76) * mm});
            skSolve(sketch);
        }
        {
            var Q0;
            Q0 = qSketchRegion(id + "F37", true);
            var Q1;
            Q1=makeQuery(id+"F26.boolean.opBoolean","MERGE",FACE,{"derivedFrom":[makeQuery(id+"F24.opExtrude","SWEPT_FACE",FACE,{"disambiguationData":[OSD([sQuery(id+"F23.wireOp",EDGE,"E66")])]}),makeQuery(id+"F26.opExtrude","SWEPT_FACE",FACE,{"disambiguationData":[OSD([sQuery(id+"F25.wireOp",EDGE,"E70.left")])]})]});
            extrude(context, id + "F38", {"entities" : qUnion([Q0]), "operationType" : NewBodyOperationType.ADD, "endBound" : BoundingType.UP_TO_SURFACE, "oppositeDirection" : true, "endBoundEntityFace" : qUnion([Q1]), "depth" : 25 * mm});
        }
    });
